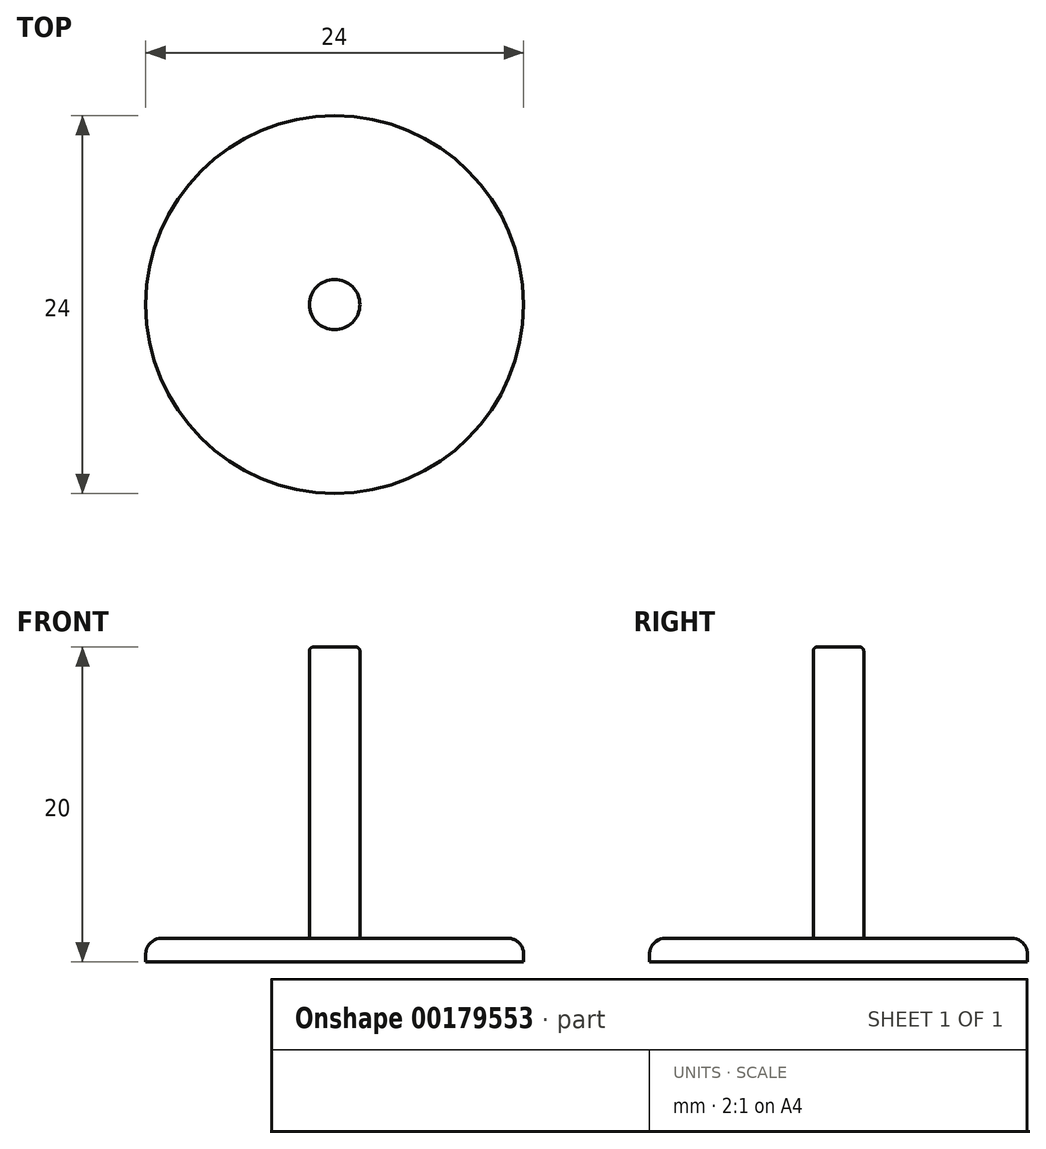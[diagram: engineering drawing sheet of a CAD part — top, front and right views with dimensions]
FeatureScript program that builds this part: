
annotation { "Feature Type Name" : "Feature", "Feature Type Description" : "" }
export const myFeature = defineFeature(function(context is Context, id is Id, definition is map)
    precondition{}
    {
        {
            var Q0;
            Q0=qCreatedBy(makeId("Top.planeOp"),FACE);
            var sketch = newSketch(context, id + "F0", { "sketchPlane" : qUnion([Q0])});
            skCircle(sketch, "E0", {"center": v(0, 0) * mm, "radius": 12 * mm});
            skCircle(sketch, "E1", {"center": v(0, 0) * mm, "radius": 1.6 * mm});
            skSolve(sketch);
        }
        {
            var Q0;
            Q0=makeQuery(id+"F0.imprint","IMPRINT",FACE,{"disambiguationData":[TD([[makeQuery(id+"F0.imprint","IMPRINT",EDGE,{"derivedFrom":sQuery(id+"F0.wireOp",EDGE,"E0")}),1.0]])]});
            extrude(context, id + "F1", {"entities" : qUnion([Q0]), "depth" : 1.5 * mm});
        }
        {
            var Q0;
            Q0=makeQuery(id+"F0.imprint","IMPRINT",FACE,{"disambiguationData":[TD([[makeQuery(id+"F0.imprint","IMPRINT",EDGE,{"derivedFrom":sQuery(id+"F0.wireOp",EDGE,"E1")}),1.0]])]});
            extrude(context, id + "F2", {"entities" : qUnion([Q0]), "operationType" : NewBodyOperationType.ADD, "depth" : 20 * mm});
        }
        {
            var Q0;
            Q0=makeQuery(id+"F1.opExtrude","CAP_EDGE",EDGE,{"disambiguationData":[OSD([sQuery(id+"F0.wireOp",EDGE,"E0")])],"isStart":false});
            var Q1;
            Q1=makeQuery(id+"F1.opExtrude","CAP_EDGE",EDGE,{"disambiguationData":[OSD([sQuery(id+"F0.wireOp",EDGE,"E1")])],"isStart":false});
            fillet(context, id + "F3", {"entities" : qUnion([Q0, Q1]), "radius" : 1 * mm, "tangentPropagation" : true, "allowEdgeOverflow" : false});
        }
        {
            var Q0;
            Q0=makeQuery(id+"F2.opExtrude","CAP_EDGE",EDGE,{"disambiguationData":[OSD([sQuery(id+"F0.wireOp",EDGE,"E1")])],"isStart":false});
            fillet(context, id + "F4", {"entities" : qUnion([Q0]), "radius" : .25 * mm, "tangentPropagation" : true, "allowEdgeOverflow" : false});
        }
    });
